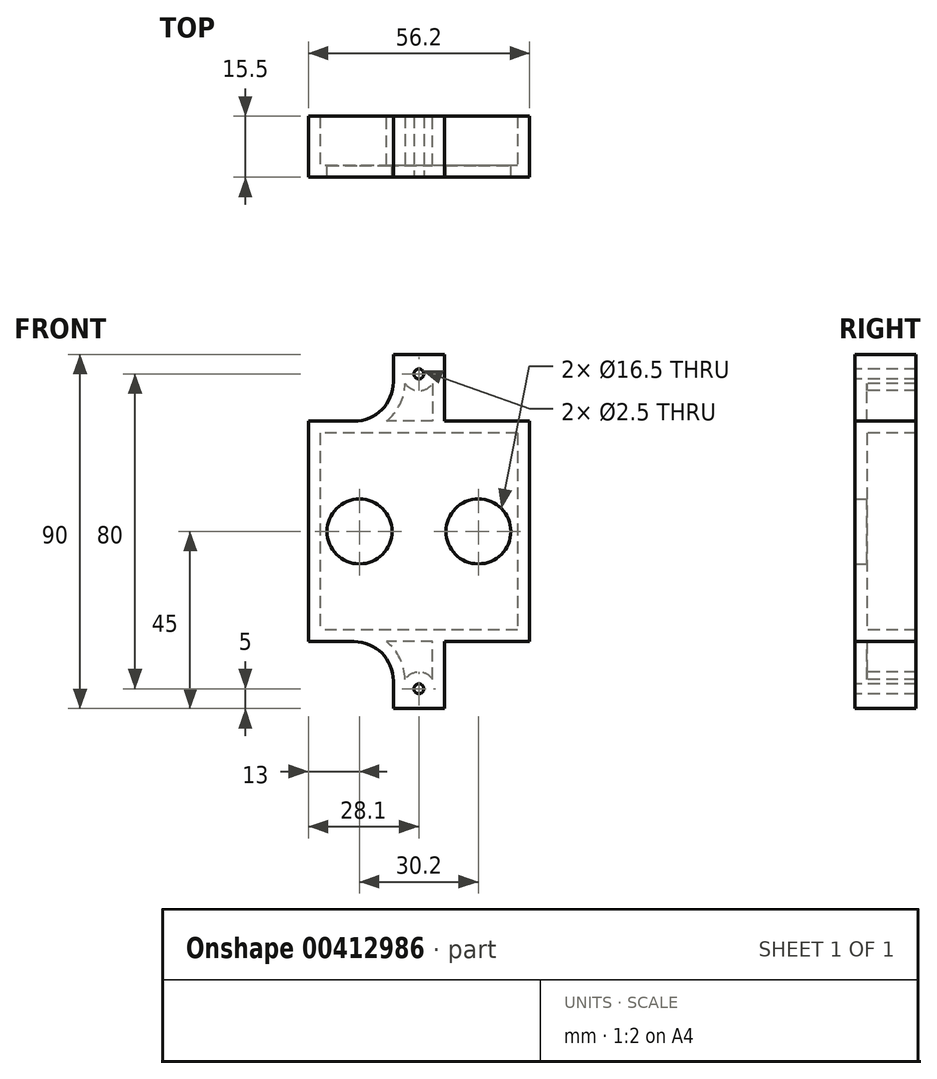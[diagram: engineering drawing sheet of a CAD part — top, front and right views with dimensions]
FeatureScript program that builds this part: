
annotation { "Feature Type Name" : "Feature", "Feature Type Description" : "" }
export const myFeature = defineFeature(function(context is Context, id is Id, definition is map)
    precondition{}
    {
        {
            var Q0;
            Q0=qCreatedBy(makeId("Front.planeOp"),FACE);
            var sketch = newSketch(context, id + "F0", { "sketchPlane" : qUnion([Q0])});
            skLineSegment(sketch, "E0.bottom", {"start": v(25.1, 25) * mm, "end": v(-25.1, 25) * mm});
            skLineSegment(sketch, "E0.top", {"start": v(25.1, -25) * mm, "end": v(-25.1, -25) * mm});
            skLineSegment(sketch, "E0.left", {"start": v(25.1, 25) * mm, "end": v(25.1, -25) * mm});
            skLineSegment(sketch, "E0.right", {"start": v(-25.1, 25) * mm, "end": v(-25.1, -25) * mm});
            skPoint(sketch, "E0.middle", {"position": v(0, 0) * mm});
            skLineSegment(sketch, "E1", {"start": v(0, 25) * mm, "end": v(0, -25) * mm, "construction": true});
            skLineSegment(sketch, "E2", {"start": v(-25.1, 0) * mm, "end": v(25.1, 0) * mm, "construction": true});
            skCircle(sketch, "E3", {"center": v(-15.1, 0) * mm, "radius": 8.25 * mm});
            skCircle(sketch, "E4.MirrorC", {"center": v(15.1, 0) * mm, "radius": 8.25 * mm});
            skLineSegment(sketch, "E5.0", {"start": v(28.1, 28) * mm, "end": v(-28.1, 28) * mm});
            skLineSegment(sketch, "E5.1", {"start": v(28.1, 28) * mm, "end": v(28.1, -28) * mm});
            skLineSegment(sketch, "E5.2", {"start": v(28.1, -28) * mm, "end": v(-28.1, -28) * mm});
            skLineSegment(sketch, "E5.3", {"start": v(-28.1, 28) * mm, "end": v(-28.1, -28) * mm});
            skSolve(sketch);
        }
        {
            var Q0;
            Q0=makeQuery(id+"F0.imprint","IMPRINT",FACE,{"disambiguationData":[TD([[makeQuery(id+"F0.imprint","IMPRINT",EDGE,{"derivedFrom":sQuery(id+"F0.wireOp",EDGE,"E0.bottom")}),1.0]])]});
            var Q1;
            Q1=makeQuery(id+"F0.imprint","IMPRINT",FACE,{"disambiguationData":[TD([[makeQuery(id+"F0.imprint","IMPRINT",EDGE,{"derivedFrom":sQuery(id+"F0.wireOp",EDGE,"E0.bottom")}),-1.0]])]});
            extrude(context, id + "F1", {"entities" : qUnion([Q0, Q1]), "depth" : 3 * mm});
        }
        {
            var Q0;
            Q0=makeQuery(id+"F0.imprint","IMPRINT",FACE,{"disambiguationData":[TD([[makeQuery(id+"F0.imprint","IMPRINT",EDGE,{"derivedFrom":sQuery(id+"F0.wireOp",EDGE,"E0.bottom")}),-1.0]])]});
            extrude(context, id + "F2", {"entities" : qUnion([Q0]), "operationType" : NewBodyOperationType.ADD, "oppositeDirection" : true, "depth" : 12.5 * mm});
        }
        {
            var Q0;
            Q0=makeQuery(id+"F1.opExtrude","CAP_FACE",FACE,{"disambiguationData":[OSD([sQuery(id+"F0.wireOp",EDGE,"E3"),sQuery(id+"F0.wireOp",EDGE,"E4.MirrorC"),sQuery(id+"F0.wireOp",EDGE,"E5.0"),sQuery(id+"F0.wireOp",EDGE,"E5.1"),sQuery(id+"F0.wireOp",EDGE,"E5.2"),sQuery(id+"F0.wireOp",EDGE,"E5.3")])],"isStart":false});
            var sketch = newSketch(context, id + "F3", { "sketchPlane" : qUnion([Q0])});
            skLineSegment(sketch, "E6.bottom", {"start": v(-6.5, 28) * mm, "end": v(6.5, 28) * mm});
            skLineSegment(sketch, "E6.top", {"start": v(-6.5, 45) * mm, "end": v(6.5, 45) * mm});
            skLineSegment(sketch, "E6.left", {"start": v(6.5, 28) * mm, "end": v(6.5, 45) * mm});
            skLineSegment(sketch, "E6.right", {"start": v(-6.5, 28) * mm, "end": v(-6.5, 45) * mm});
            skLineSegment(sketch, "E7", {"start": v(0, 45) * mm, "end": v(0, 28) * mm, "construction": true});
            skLineSegment(sketch, "E8.bottom", {"start": v(38.34, 45) * mm, "end": v(-38.34, 45) * mm, "construction": true});
            skLineSegment(sketch, "E8.top", {"start": v(38.34, -45) * mm, "end": v(-38.34, -45) * mm, "construction": true});
            skLineSegment(sketch, "E8.left", {"start": v(38.34, 45) * mm, "end": v(38.34, -45) * mm, "construction": true});
            skLineSegment(sketch, "E8.right", {"start": v(-38.34, 45) * mm, "end": v(-38.34, -45) * mm, "construction": true});
            skPoint(sketch, "E8.middle", {"position": v(0, 0) * mm});
            skCircle(sketch, "E9", {"center": v(0, 40) * mm, "radius": 1.25 * mm});
            skLineSegment(sketch, "E10.MirrorCS", {"start": v(-6.5, -28) * mm, "end": v(6.5, -28) * mm});
            skLineSegment(sketch, "E11.MirrorCS", {"start": v(-6.5, -28) * mm, "end": v(-6.5, -45) * mm});
            skLineSegment(sketch, "E12.MirrorCS", {"start": v(-6.5, -45) * mm, "end": v(6.5, -45) * mm});
            skLineSegment(sketch, "E13.MirrorCS", {"start": v(6.5, -28) * mm, "end": v(6.5, -45) * mm});
            skCircle(sketch, "E14.MirrorC", {"center": v(0, -40) * mm, "radius": 1.25 * mm});
            skSolve(sketch);
        }
        {
            var Q0;
            Q0=makeQuery(id+"F3.imprint","IMPRINT",FACE,{"disambiguationData":[TD([[makeQuery(id+"F3.imprint","IMPRINT",EDGE,{"derivedFrom":sQuery(id+"F3.wireOp",EDGE,"E6.bottom")}),-1.0]])]});
            var Q1;
            Q1=makeQuery(id+"F3.imprint","IMPRINT",FACE,{"disambiguationData":[TD([[makeQuery(id+"F3.imprint","IMPRINT",EDGE,{"derivedFrom":sQuery(id+"F3.wireOp",EDGE,"E10.MirrorCS")}),1.0]])]});
            var Q2;
            Q2=makeQuery(id+"F2.opExtrude","CAP_FACE",FACE,{"disambiguationData":[OSD([sQuery(id+"F0.wireOp",EDGE,"E0.bottom"),sQuery(id+"F0.wireOp",EDGE,"E0.top"),sQuery(id+"F0.wireOp",EDGE,"E0.left"),sQuery(id+"F0.wireOp",EDGE,"E0.right"),sQuery(id+"F0.wireOp",EDGE,"E5.0"),sQuery(id+"F0.wireOp",EDGE,"E5.1"),sQuery(id+"F0.wireOp",EDGE,"E5.2"),sQuery(id+"F0.wireOp",EDGE,"E5.3")])],"isStart":false});
            extrude(context, id + "F4", {"entities" : qUnion([Q0, Q1]), "operationType" : NewBodyOperationType.ADD, "endBound" : BoundingType.UP_TO_SURFACE, "oppositeDirection" : true, "endBoundEntityFace" : qUnion([Q2]), "depth" : 12.75 * mm});
        }
        {
            var Q0;
            Q0=makeQuery(id+"F4.opExtrude","SWEPT_EDGE",EDGE,{"disambiguationData":[OSD([sQuery(id+"F0.wireOp",EDGE,"E5.2"),sQuery(id+"F3.wireOp",EDGE,"E10.MirrorCS"),sQuery(id+"F3.wireOp",EDGE,"E13.MirrorCS")])]});
            var Q1;
            Q1=makeQuery(id+"F4.opExtrude","SWEPT_EDGE",EDGE,{"disambiguationData":[OSD([sQuery(id+"F0.wireOp",EDGE,"E5.2"),sQuery(id+"F3.wireOp",EDGE,"E10.MirrorCS"),sQuery(id+"F3.wireOp",EDGE,"E11.MirrorCS")])]});
            var Q2;
            Q2=makeQuery(id+"F4.opExtrude","SWEPT_EDGE",EDGE,{"disambiguationData":[OSD([sQuery(id+"F0.wireOp",EDGE,"E5.0"),sQuery(id+"F3.wireOp",EDGE,"E6.bottom"),sQuery(id+"F3.wireOp",EDGE,"E6.right")])]});
            var Q3;
            Q3=makeQuery(id+"F4.opExtrude","SWEPT_EDGE",EDGE,{"disambiguationData":[OSD([sQuery(id+"F0.wireOp",EDGE,"E5.0"),sQuery(id+"F3.wireOp",EDGE,"E6.bottom"),sQuery(id+"F3.wireOp",EDGE,"E6.left")])]});
            fillet(context, id + "F5", {"entities" : qUnion([Q0, Q1, Q2, Q3]), "radius" : 10 * mm, "tangentPropagation" : true, "allowEdgeOverflow" : false});
        }
        {
            var Q0;
            {var subQ0=sQuery(id+"F0.wireOp",EDGE,"E5.3");var subQ1=sQuery(id+"F0.wireOp",EDGE,"E5.2");var subQ2=sQuery(id+"F0.wireOp",EDGE,"E5.1");var subQ3=sQuery(id+"F0.wireOp",EDGE,"E5.0");var subQ4=sQuery(id+"F0.wireOp",EDGE,"E0.right");var subQ5=sQuery(id+"F0.wireOp",EDGE,"E0.left");var subQ6=sQuery(id+"F0.wireOp",EDGE,"E0.top");var subQ7=sQuery(id+"F0.wireOp",EDGE,"E0.bottom");Q0=makeQuery(id+"F4.boolean.opBoolean","MERGE",FACE,{"derivedFrom":[makeQuery(id+"F2.opExtrude","CAP_FACE",FACE,{"disambiguationData":[OSD([subQ7,subQ6,subQ5,subQ4,subQ3,subQ2,subQ1,subQ0])],"isStart":false}),makeQuery(id+"F4.opExtrude","CAP_FACE",FACE,{"disambiguationData":[OSD([subQ7,subQ6,subQ5,subQ4,subQ3,subQ2,subQ1,subQ0]),ownerDisambiguation([makeQuery(id+"F3.imprint","IMPRINT",EDGE,{"derivedFrom":sQuery(id+"F3.wireOp",EDGE,"E6.bottom")})])],"isStart":false}),makeQuery(id+"F4.opExtrude","CAP_FACE",FACE,{"disambiguationData":[OSD([subQ7,subQ6,subQ5,subQ4,subQ3,subQ2,subQ1,subQ0]),ownerDisambiguation([makeQuery(id+"F3.imprint","IMPRINT",EDGE,{"derivedFrom":sQuery(id+"F3.wireOp",EDGE,"E10.MirrorCS")})])],"isStart":false})]});}
            shell(context, id + "F6", {"entities" : qUnion([Q0]), "thickness" : 3 * mm});
        }
    });
